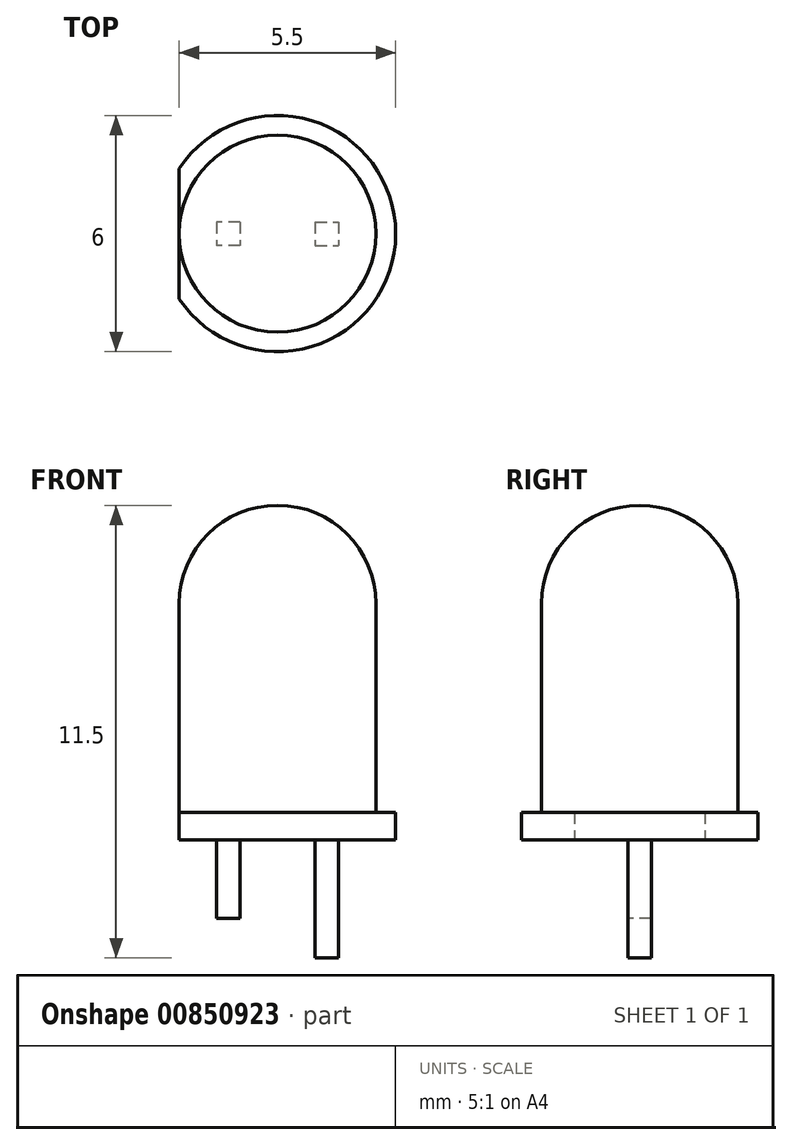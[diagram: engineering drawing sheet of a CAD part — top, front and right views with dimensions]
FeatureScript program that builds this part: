
annotation { "Feature Type Name" : "Feature", "Feature Type Description" : "" }
export const myFeature = defineFeature(function(context is Context, id is Id, definition is map)
    precondition{}
    {
        {
            var Q0;
            Q0=qCreatedBy(makeId("Top.planeOp"),FACE);
            var sketch = newSketch(context, id + "F0", { "sketchPlane" : qUnion([Q0])});
            skCircle(sketch, "E0", {"center": v(0, 0) * mm, "radius": 2.5 * mm});
            skSolve(sketch);
        }
        {
            var Q0;
            Q0=qSketchRegion(id+"F0",true);
            extrude(context, id + "F1", {"entities" : qUnion([Q0]), "depth" : 6 * mm});
        }
        {
            var Q0;
            Q0=makeQuery(id+"F1.opExtrude","CAP_FACE",FACE,{"disambiguationData":[OSD([sQuery(id+"F0.wireOp",EDGE,"E0")])],"isStart":false});
            var sketch = newSketch(context, id + "F2", { "sketchPlane" : qUnion([Q0])});
            skLineSegment(sketch, "E1", {"start": v(0, -2.5) * mm, "end": v(0, 2.5) * mm});
            skArc(sketch, "E2", {"start": v(0, 2.5) * mm, "mid": v(-2.5, 0) * mm, "end": v(0, -2.5) * mm});
            skSolve(sketch);
        }
        {
            var Q0;
            Q0=qSketchRegion(id+"F2",true);
            var Q1;
            Q1=sQuery(id+"F2.wireOp",EDGE,"E1");
            revolve(context, id + "F3", {"operationType" : NewBodyOperationType.ADD, "entities" : qUnion([Q0]), "axis" : qUnion([Q1]), "revolveType" : RevolveType.FULL});
        }
        {
            var Q0;
            Q0=makeQuery(id+"F1.opExtrude","CAP_FACE",FACE,{"disambiguationData":[OSD([sQuery(id+"F0.wireOp",EDGE,"E0")])],"isStart":true});
            var sketch = newSketch(context, id + "F4", { "sketchPlane" : qUnion([Q0])});
            skArc(sketch, "E3.0", {"start": v(-2.5, -1.66) * mm, "mid": v(3, 0) * mm, "end": v(-2.5, 1.66) * mm});
            skLineSegment(sketch, "E4", {"start": v(-2.5, -1.66) * mm, "end": v(-2.5, 1.66) * mm});
            skSolve(sketch);
        }
        {
            var Q0;
            Q0=qSketchRegion(id+"F4",true);
            extrude(context, id + "F5", {"entities" : qUnion([Q0]), "operationType" : NewBodyOperationType.ADD, "oppositeDirection" : true, "depth" : .7 * mm});
        }
        {
            var Q0;
            Q0=makeQuery(id+"F5.boolean.opBoolean","MERGE",FACE,{"derivedFrom":[makeQuery(id+"F1.opExtrude","CAP_FACE",FACE,{"disambiguationData":[OSD([sQuery(id+"F0.wireOp",EDGE,"E0")])],"isStart":true}),makeQuery(id+"F5.opExtrude","CAP_FACE",FACE,{"disambiguationData":[OSD([sQuery(id+"F4.wireOp",EDGE,"E3.0"),sQuery(id+"F4.wireOp",EDGE,"E4")])],"isStart":true})]});
            var sketch = newSketch(context, id + "F6", { "sketchPlane" : qUnion([Q0])});
            skLineSegment(sketch, "E5.rect.bottom", {"start": v(0.95, -0.3) * mm, "end": v(1.55, -0.3) * mm});
            skLineSegment(sketch, "E5.rect.top", {"start": v(0.95, 0.3) * mm, "end": v(1.55, 0.3) * mm});
            skLineSegment(sketch, "E5.rect.left", {"start": v(0.95, -0.3) * mm, "end": v(0.95, 0.3) * mm});
            skLineSegment(sketch, "E5.rect.right", {"start": v(1.55, -0.3) * mm, "end": v(1.55, 0.3) * mm});
            skPoint(sketch, "E5.rect.middle", {"position": v(1.25, 0) * mm});
            skLineSegment(sketch, "E6.rect.bottom", {"start": v(-0.95, -0.3) * mm, "end": v(-1.55, -0.3) * mm});
            skLineSegment(sketch, "E6.rect.top", {"start": v(-0.95, 0.3) * mm, "end": v(-1.55, 0.3) * mm});
            skLineSegment(sketch, "E6.rect.left", {"start": v(-0.95, -0.3) * mm, "end": v(-0.95, 0.3) * mm});
            skLineSegment(sketch, "E6.rect.right", {"start": v(-1.55, -0.3) * mm, "end": v(-1.55, 0.3) * mm});
            skPoint(sketch, "E6.rect.middle", {"position": v(-1.25, 0) * mm});
            skLineSegment(sketch, "E7", {"start": v(1.55, -0.3) * mm, "end": v(0.95, 0.3) * mm, "construction": true});
            skLineSegment(sketch, "E8", {"start": v(1.55, 0.3) * mm, "end": v(0.95, -0.3) * mm, "construction": true});
            skLineSegment(sketch, "E9", {"start": v(-0.95, -0.3) * mm, "end": v(-1.55, 0.3) * mm, "construction": true});
            skLineSegment(sketch, "E10", {"start": v(-0.95, 0.3) * mm, "end": v(-1.55, -0.3) * mm, "construction": true});
            skLineSegment(sketch, "E11", {"start": v(1.25, 0) * mm, "end": v(-1.25, 0) * mm, "construction": true});
            skSolve(sketch);
        }
        {
            var Q0;
            Q0=qSketchRegion(id+"F6",true);
            extrude(context, id + "F7", {"entities" : qUnion([Q0]), "operationType" : NewBodyOperationType.ADD, "depth" : 2 * mm, "offsetDistance" : 25 * mm});
        }
        {
            var Q0;
            Q0=makeQuery(id+"F7.opExtrude","CAP_FACE",FACE,{"disambiguationData":[OSD([sQuery(id+"F6.wireOp",EDGE,"E5.rect.bottom"),sQuery(id+"F6.wireOp",EDGE,"E5.rect.top"),sQuery(id+"F6.wireOp",EDGE,"E5.rect.left"),sQuery(id+"F6.wireOp",EDGE,"E5.rect.right")])],"isStart":false});
            extrude(context, id + "F8", {"entities" : qUnion([Q0]), "operationType" : NewBodyOperationType.ADD, "depth" : 1 * mm, "offsetDistance" : 25 * mm});
        }
    });
